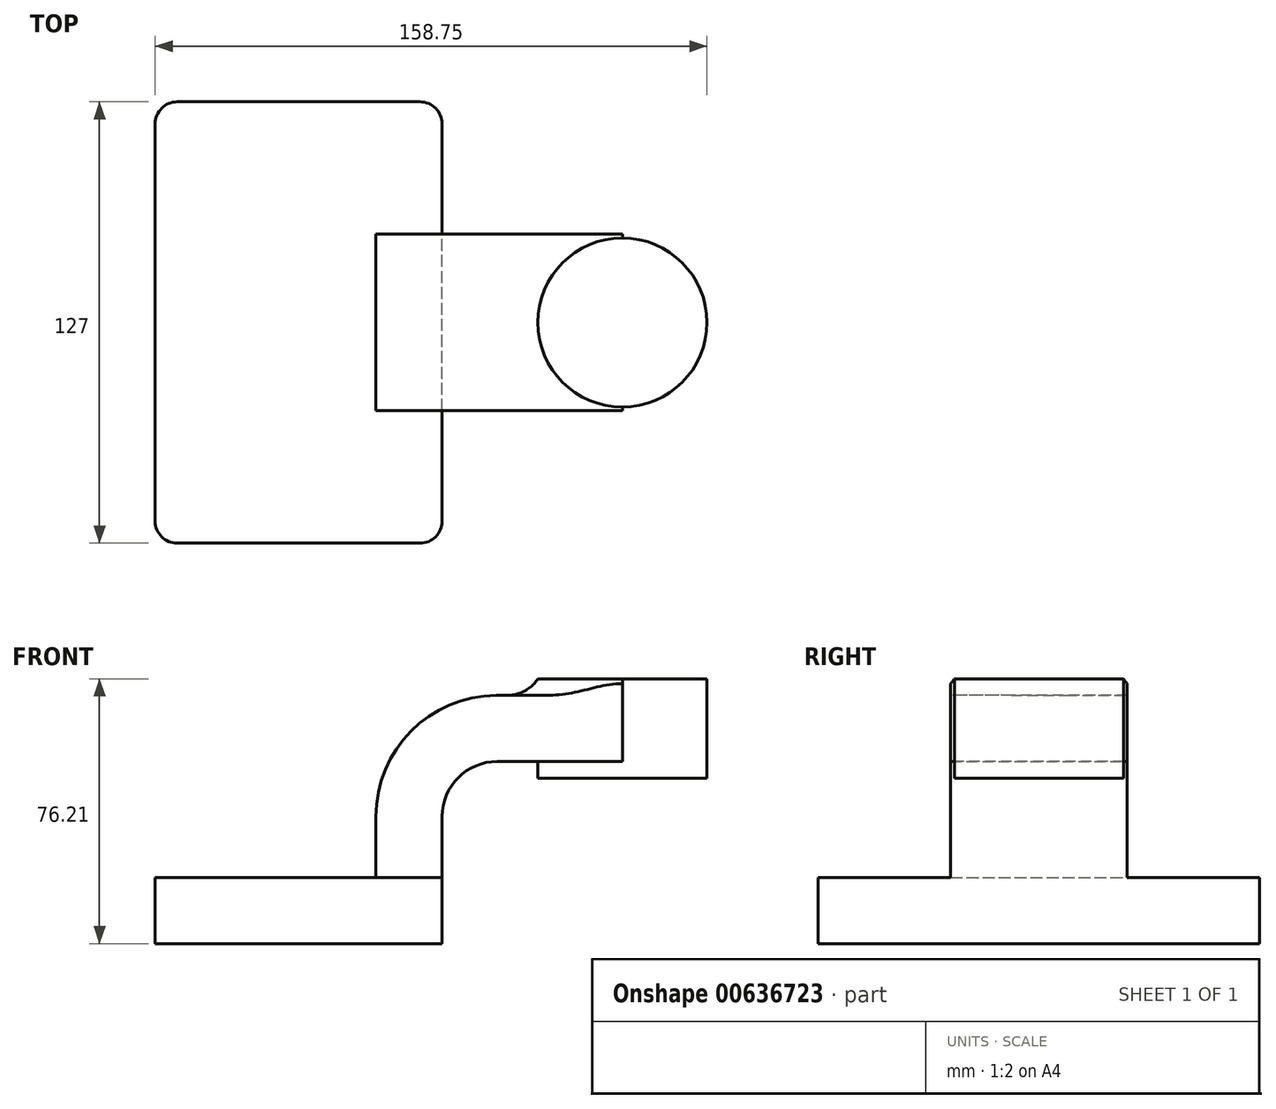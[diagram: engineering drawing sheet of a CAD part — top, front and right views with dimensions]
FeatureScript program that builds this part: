
annotation { "Feature Type Name" : "Feature", "Feature Type Description" : "" }
export const myFeature = defineFeature(function(context is Context, id is Id, definition is map)
    precondition{}
    {
        {
            var Q0;
            Q0=qCreatedBy(makeId("Front.planeOp"),FACE);
            var sketch = newSketch(context, id + "F0", { "sketchPlane" : qUnion([Q0])});
            skLineSegment(sketch, "E0.bottom", {"start": v(41.28, -9.52) * mm, "end": v(-41.28, -9.53) * mm});
            skLineSegment(sketch, "E0.top", {"start": v(41.28, 9.53) * mm, "end": v(-41.28, 9.53) * mm});
            skLineSegment(sketch, "E0.left", {"start": v(41.28, -9.52) * mm, "end": v(41.28, 9.53) * mm});
            skLineSegment(sketch, "E0.right", {"start": v(-41.28, -9.53) * mm, "end": v(-41.28, 9.53) * mm});
            skPoint(sketch, "E0.middle", {"position": v(0, 0) * mm});
            skPoint(sketch, "E1.middle", {"position": v(61.04, 49.24) * mm});
            skLineSegment(sketch, "E2.bottom", {"start": v(117.48, 38.1) * mm, "end": v(66.68, 38.1) * mm});
            skLineSegment(sketch, "E2.top", {"start": v(117.48, 66.68) * mm, "end": v(66.68, 66.68) * mm});
            skLineSegment(sketch, "E2.left", {"start": v(117.48, 38.1) * mm, "end": v(117.48, 66.68) * mm});
            skLineSegment(sketch, "E2.right", {"start": v(66.68, 38.1) * mm, "end": v(66.68, 66.68) * mm});
            skPoint(sketch, "E2.middle", {"position": v(92.08, 52.39) * mm});
            skLineSegment(sketch, "E3", {"start": v(41.28, 9.53) * mm, "end": v(41.28, 27) * mm});
            skArc(sketch, "E4", {"start": v(41.27, 27) * mm, "mid": v(45.92, 38.23) * mm, "end": v(57.15, 42.88) * mm});
            skLineSegment(sketch, "E5", {"start": v(57.15, 42.88) * mm, "end": v(93.14, 42.88) * mm});
            skLineSegment(sketch, "E6.0", {"start": v(57.15, 61.93) * mm, "end": v(93.14, 61.93) * mm});
            skArc(sketch, "E6.1", {"start": v(22.23, 27) * mm, "mid": v(32.45, 51.7) * mm, "end": v(57.15, 61.93) * mm});
            skLineSegment(sketch, "E6.2", {"start": v(22.22, 9.53) * mm, "end": v(22.22, 27) * mm});
            skLineSegment(sketch, "E7", {"start": v(93.14, 66.68) * mm, "end": v(93.14, 38.1) * mm});
            skFitSpline(sketch, "E8", {"points": [v(-41.28, 9.52) * mm, v(57.15, 61.93) * mm], "startDerivative": vector(12.95, 105.34) * mm, "endDerivative": vector(130.32, 0.36) * mm});
            skSolve(sketch);
        }
        {
            var Q0;
            Q0=makeQuery(id+"F0.imprint","IMPRINT",FACE,{"disambiguationData":[TD([[makeQuery(id+"F0.imprint","IMPRINT",EDGE,{"derivedFrom":sQuery(id+"F0.wireOp",EDGE,"E0.bottom")}),-1.0]])]});
            extrude(context, id + "F1", {"entities" : qUnion([Q0]), "endBound" : BoundingType.SYMMETRIC, "depth" : 127 * mm, "offsetDistance" : 25.4 * mm});
        }
        {
            var Q0;
            {var subQ5=sQuery(id+"F0.wireOp",EDGE,"E3");Q0=makeQuery(id+"F0.imprint","IMPRINT",FACE,{"disambiguationData":[TD([[makeQuery(id+"F0.imprint","IMPRINT",EDGE,{"derivedFrom":subQ5}),1.0]])]});}
            var Q1;
            {var subQ0=sQuery(id+"F0.wireOp",EDGE,"E5");var subQ1=sQuery(id+"F0.wireOp",EDGE,"E2.right");var subQ2=makeQuery(id+"F0.imprint","INTERSECT",VERTEX,{"derivedFrom":[subQ1,subQ0]});Q1=makeQuery(id+"F0.imprint","IMPRINT",FACE,{"disambiguationData":[TD([[makeQuery(id+"F0.imprint","IMPRINT",EDGE,{"disambiguationData":[TD([[subQ2,-1.0]])],"derivedFrom":subQ1}),-1.0]])]});}
            extrude(context, id + "F2", {"entities" : qUnion([Q0, Q1]), "operationType" : NewBodyOperationType.ADD, "endBound" : BoundingType.SYMMETRIC, "depth" : 50.8 * mm, "offsetDistance" : 25.4 * mm});
        }
        {
            var Q0;
            {var subQ4=sQuery(id+"F0.wireOp",EDGE,"E6.1");Q0=makeQuery(id+"F0.imprint","IMPRINT",FACE,{"disambiguationData":[TD([[makeQuery(id+"F0.imprint","IMPRINT",EDGE,{"derivedFrom":subQ4}),1.0]])]});}
            extrude(context, id + "F3", {"entities" : qUnion([Q0]), "operationType" : NewBodyOperationType.ADD, "endBound" : BoundingType.SYMMETRIC, "depth" : 15.88 * mm, "offsetDistance" : 25.4 * mm});
        }
        {
            var Q0;
            {var subQ4=sQuery(id+"F0.wireOp",EDGE,"E2.left");Q0=makeQuery(id+"F0.imprint","IMPRINT",FACE,{"disambiguationData":[TD([[makeQuery(id+"F0.imprint","IMPRINT",EDGE,{"derivedFrom":subQ4}),1.0]])]});}
            var Q1;
            Q1=sQuery(id+"F0.wireOp",EDGE,"E7");
            revolve(context, id + "F4", {"operationType" : NewBodyOperationType.ADD, "entities" : qUnion([Q0]), "axis" : qUnion([Q1]), "revolveType" : RevolveType.FULL});
        }
        {
            var Q0;
            Q0=makeQuery(id+"F1.opExtrude","CAP_EDGE",EDGE,{"disambiguationData":[OSD([sQuery(id+"F0.wireOp",EDGE,"E0.right")])],"isStart":true});
            var Q1;
            Q1=makeQuery(id+"F1.opExtrude","CAP_EDGE",EDGE,{"disambiguationData":[OSD([sQuery(id+"F0.wireOp",EDGE,"E0.right")])],"isStart":false});
            var Q2;
            Q2=makeQuery(id+"F1.opExtrude","CAP_EDGE",EDGE,{"disambiguationData":[OSD([sQuery(id+"F0.wireOp",EDGE,"E0.left")])],"isStart":false});
            var Q3;
            Q3=makeQuery(id+"F1.opExtrude","CAP_EDGE",EDGE,{"disambiguationData":[OSD([sQuery(id+"F0.wireOp",EDGE,"E0.left")])],"isStart":true});
            fillet(context, id + "F5", {"entities" : qUnion([Q0, Q1, Q2, Q3]), "radius" : 6.35 * mm, "tangentPropagation" : true, "allowEdgeOverflow" : false});
        }
        {
            var Q0;
            Q0=makeQuery(id+"F4.boolean.opBoolean","INTERSECT",EDGE,{"derivedFrom":[makeQuery(id+"F2.opExtrude","SWEPT_FACE",FACE,{"disambiguationData":[OSD([sQuery(id+"F0.wireOp",EDGE,"E6.0")])]}),makeQuery(id+"F4.opRevolve","SWEPT_FACE",FACE,{"disambiguationData":[OSD([sQuery(id+"F0.wireOp",EDGE,"E2.left")])]})]});
            fillet(context, id + "F6", {"entities" : qUnion([Q0]), "radius" : 10.16 * mm, "tangentPropagation" : true, "allowEdgeOverflow" : false});
        }
    });
